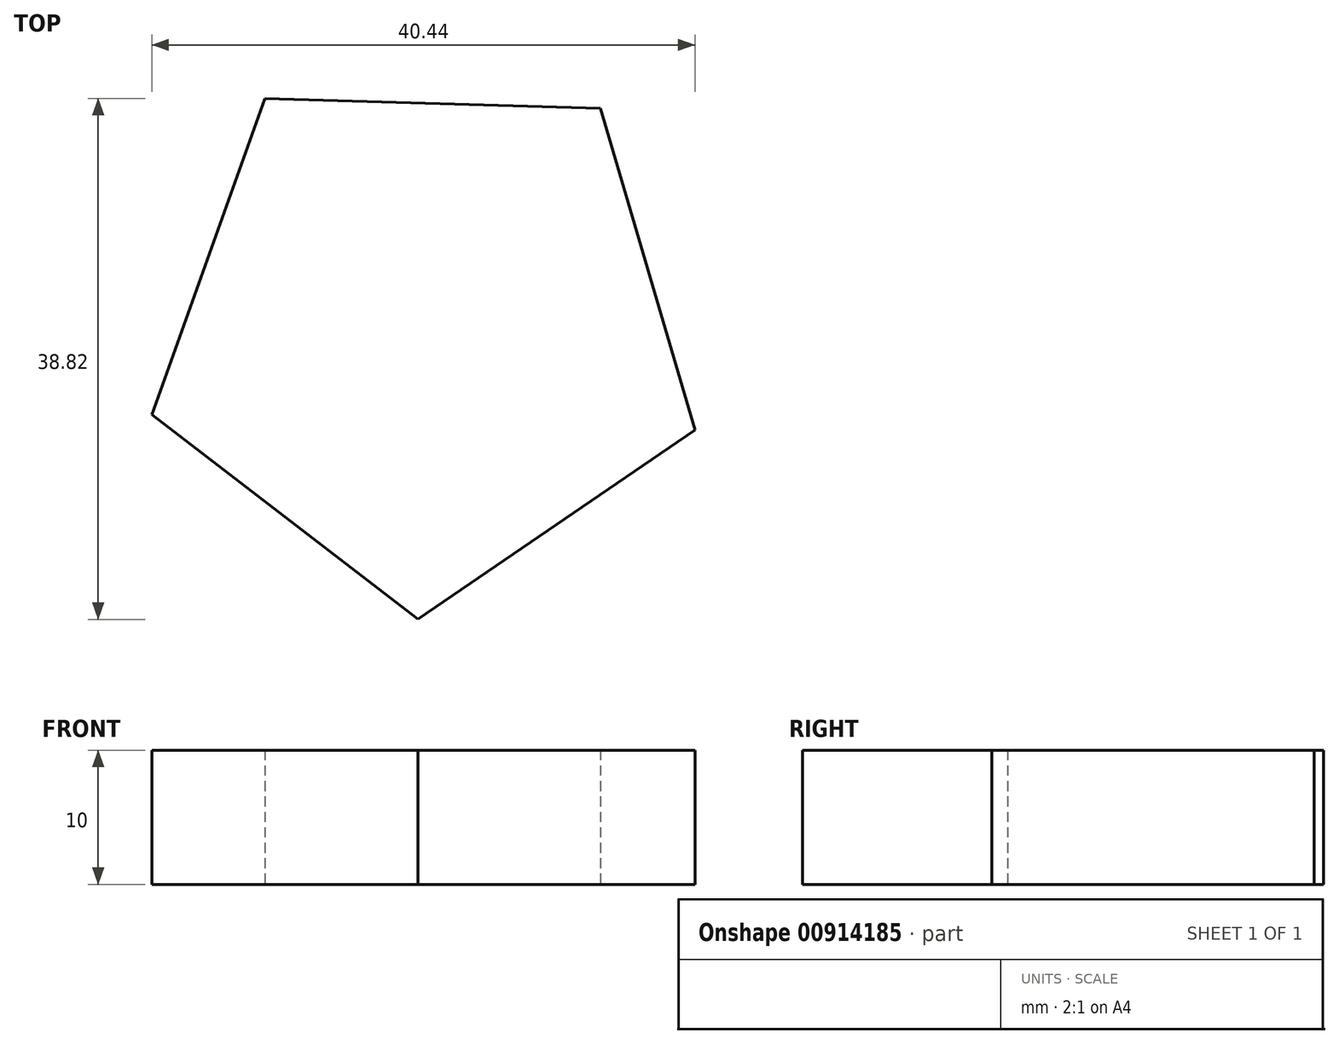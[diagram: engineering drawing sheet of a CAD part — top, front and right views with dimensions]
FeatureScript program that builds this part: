
annotation { "Feature Type Name" : "Feature", "Feature Type Description" : "" }
export const myFeature = defineFeature(function(context is Context, id is Id, definition is map)
    precondition{}
    {
        {
            var Q0;
            Q0=qCreatedBy(makeId("Top.planeOp"),FACE);
            var sketch = newSketch(context, id + "F0", { "sketchPlane" : qUnion([Q0])});
            skCircle(sketch, "E0.cCircle", {"center": v(0, 0) * mm, "radius": 17.2 * mm, "construction": true});
            skLineSegment(sketch, "E0.0", {"start": v(20.03, -7.15) * mm, "end": v(-0.6, -21.26) * mm});
            skLineSegment(sketch, "E0.1", {"start": v(-0.6, -21.26) * mm, "end": v(-20.4, -6) * mm});
            skLineSegment(sketch, "E0.2", {"start": v(-20.4, -6) * mm, "end": v(-12, 17.56) * mm});
            skLineSegment(sketch, "E0.3", {"start": v(-12, 17.56) * mm, "end": v(12.99, 16.84) * mm});
            skLineSegment(sketch, "E0.4", {"start": v(12.99, 16.84) * mm, "end": v(20.03, -7.15) * mm});
            skPoint(sketch, "E0.0.midPoint", {"position": v(9.71, -14.2) * mm});
            skSolve(sketch);
        }
        {
            var Q0;
            Q0=makeQuery(id+"F0.imprint","IMPRINT",FACE,{"disambiguationData":[TD([[makeQuery(id+"F0.imprint","IMPRINT",EDGE,{"derivedFrom":sQuery(id+"F0.wireOp",EDGE,"E0.0")}),-1.0]])]});
            extrude(context, id + "F1", {"entities" : qUnion([Q0]), "depth" : 10 * mm, "offsetDistance" : 25 * mm});
        }
    });
